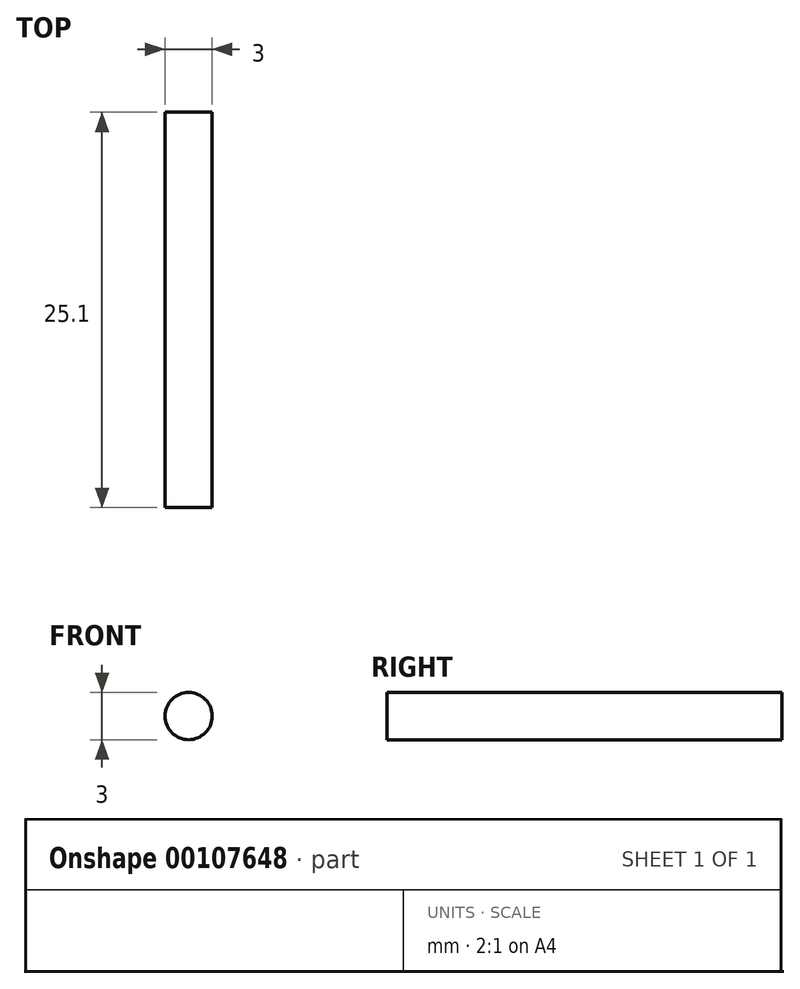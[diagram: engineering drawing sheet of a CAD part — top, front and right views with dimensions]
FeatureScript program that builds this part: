
annotation { "Feature Type Name" : "Feature", "Feature Type Description" : "" }
export const myFeature = defineFeature(function(context is Context, id is Id, definition is map)
    precondition{}
    {
        {
            var Q0;
            Q0=qCreatedBy(makeId("Front.planeOp"),FACE);
            var sketch = newSketch(context, id + "F0", { "sketchPlane" : qUnion([Q0])});
            skCircle(sketch, "E0", {"center": v(0, 0) * mm, "radius": 1.5 * mm});
            skSolve(sketch);
        }
        {
            var Q0;
            Q0=makeQuery(id+"F0.imprint","IMPRINT",FACE,{"disambiguationData":[TD([[makeQuery(id+"F0.imprint","IMPRINT",EDGE,{"derivedFrom":sQuery(id+"F0.wireOp",EDGE,"E0")}),1.0]])]});
            extrude(context, id + "F1", {"entities" : qUnion([Q0]), "depth" : 25.1 * mm});
        }
    });
